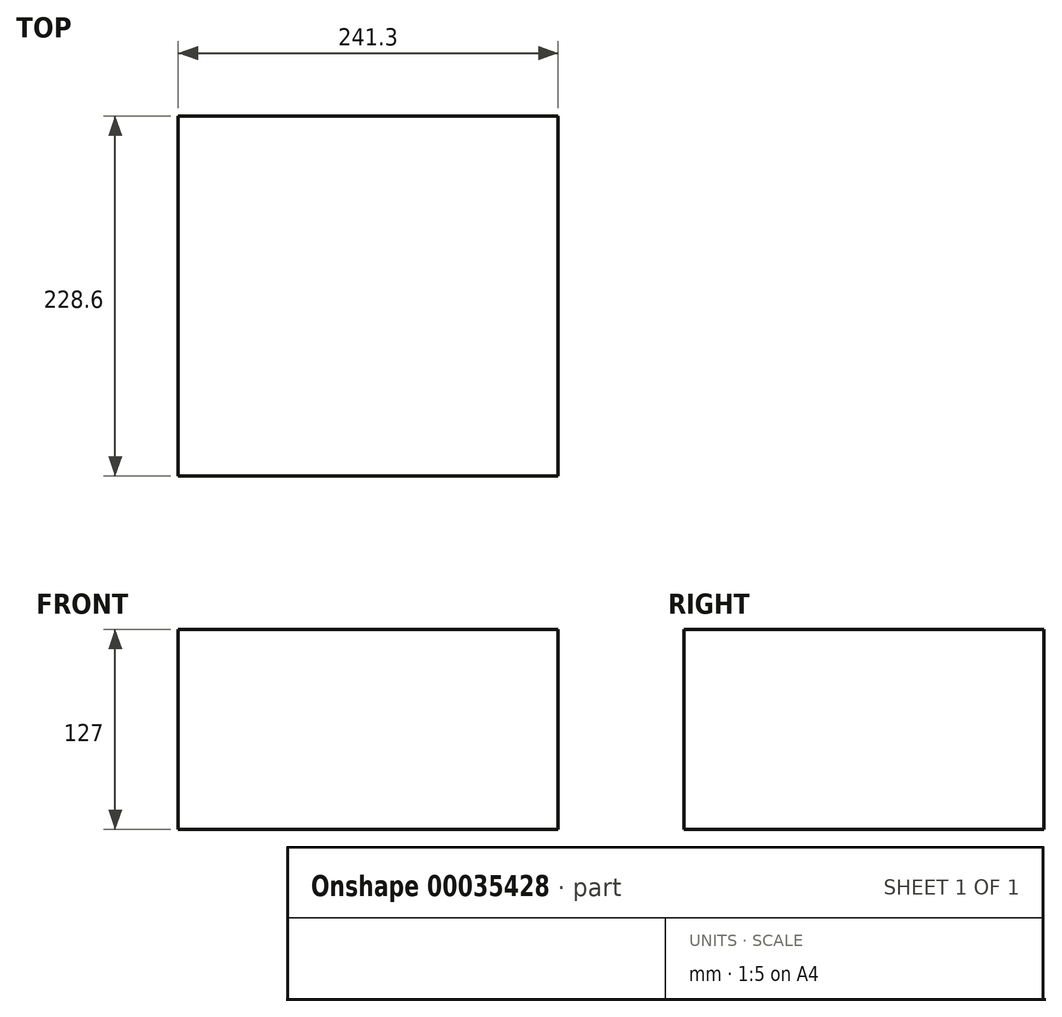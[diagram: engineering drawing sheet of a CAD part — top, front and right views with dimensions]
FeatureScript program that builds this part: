
annotation { "Feature Type Name" : "Feature", "Feature Type Description" : "" }
export const myFeature = defineFeature(function(context is Context, id is Id, definition is map)
    precondition{}
    {
        {
            var Q0;
            Q0=qCreatedBy(makeId("Top.planeOp"),FACE);
            var sketch = newSketch(context, id + "F0", { "sketchPlane" : qUnion([Q0])});
            skLineSegment(sketch, "E0.rect.bottom", {"start": v(120.65, 114.3) * mm, "end": v(-120.65, 114.3) * mm});
            skLineSegment(sketch, "E0.rect.top", {"start": v(120.65, -114.3) * mm, "end": v(-120.65, -114.3) * mm});
            skLineSegment(sketch, "E0.rect.left", {"start": v(120.65, 114.3) * mm, "end": v(120.65, -114.3) * mm});
            skLineSegment(sketch, "E0.rect.right", {"start": v(-120.65, 114.3) * mm, "end": v(-120.65, -114.3) * mm});
            skPoint(sketch, "E0.rect.middle", {"position": v(0, 0) * mm});
            skSolve(sketch);
        }
        {
            var Q0;
            Q0=makeQuery(id+"F0.imprint","IMPRINT",FACE,{"disambiguationData":[TD([[makeQuery(id+"F0.imprint","IMPRINT",EDGE,{"derivedFrom":sQuery(id+"F0.wireOp",EDGE,"E0.rect.bottom")}),1.0]])]});
            extrude(context, id + "F1", {"entities" : qUnion([Q0]), "depth" : 127 * mm});
        }
    });
